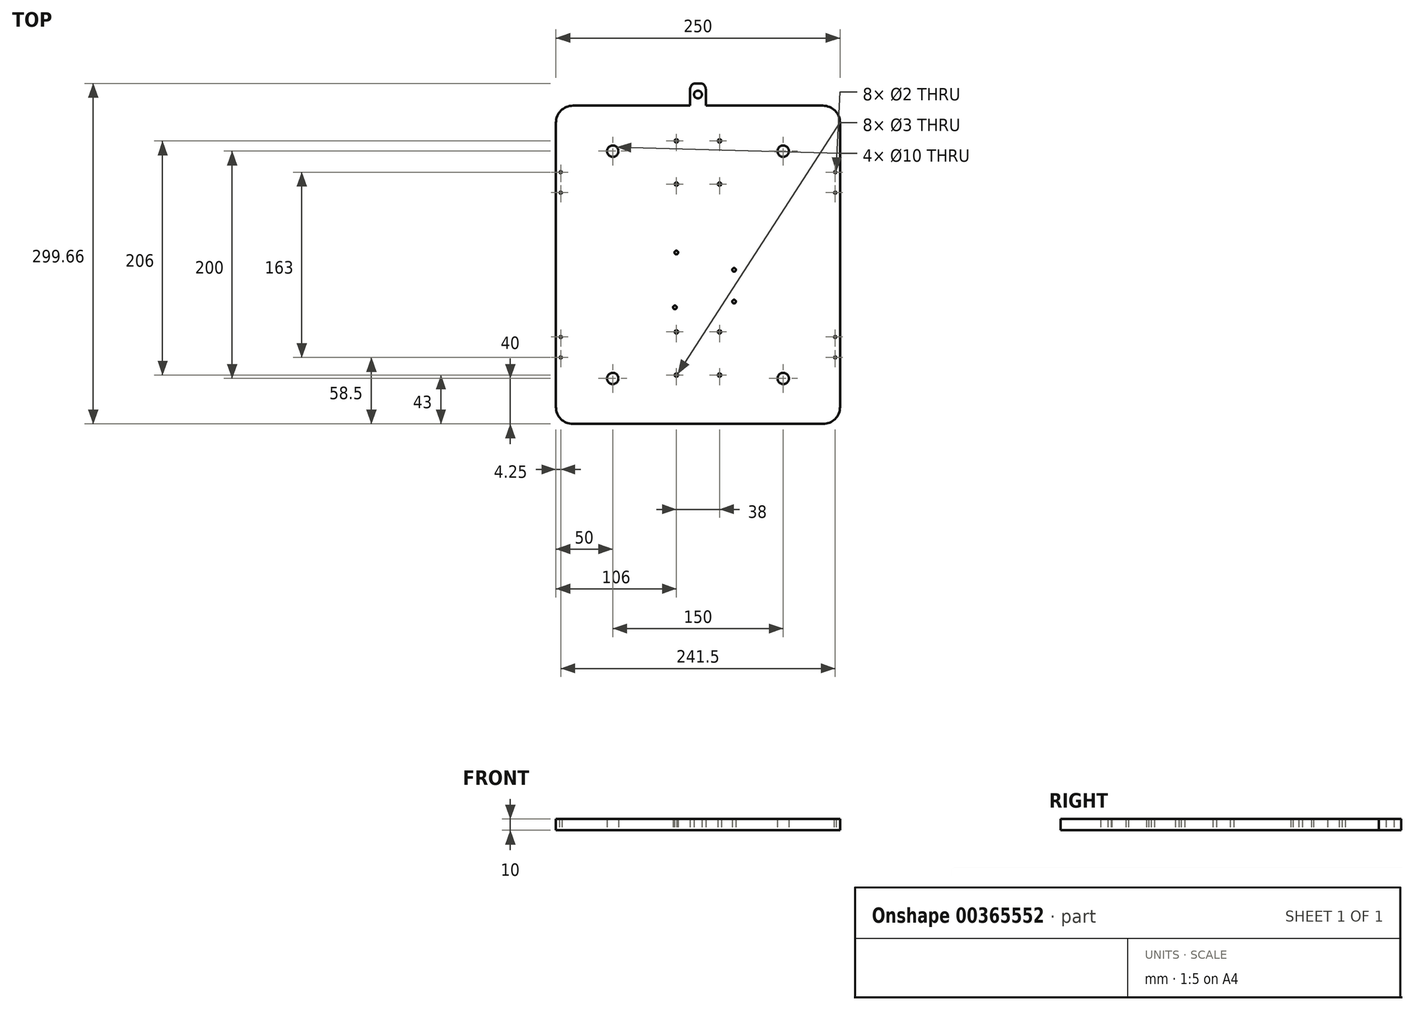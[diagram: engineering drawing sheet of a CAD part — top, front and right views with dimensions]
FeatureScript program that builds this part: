
annotation { "Feature Type Name" : "Feature", "Feature Type Description" : "" }
export const myFeature = defineFeature(function(context is Context, id is Id, definition is map)
    precondition{}
    {
        {
            var Q0;
            Q0=qCreatedBy(makeId("Top.planeOp"),FACE);
            var sketch = newSketch(context, id + "F0", { "sketchPlane" : qUnion([Q0])});
            skLineSegment(sketch, "E0.bottom", {"start": v(34.5, 17) * mm, "end": v(-34.5, 17) * mm});
            skLineSegment(sketch, "E0.top", {"start": v(34.5, -17) * mm, "end": v(-34.5, -17) * mm});
            skLineSegment(sketch, "E0.left", {"start": v(34.5, 17) * mm, "end": v(34.5, -17) * mm});
            skLineSegment(sketch, "E0.right", {"start": v(-34.5, 17) * mm, "end": v(-34.5, -17) * mm});
            skPoint(sketch, "E0.middle", {"position": v(0, 0) * mm});
            skSolve(sketch);
        }
        {
            var Q0;
            Q0=qCreatedBy(makeId("Top.planeOp"),FACE);
            var sketch = newSketch(context, id + "F1", { "sketchPlane" : qUnion([Q0])});
            skLineSegment(sketch, "E1.bottom", {"start": v(-110, 140) * mm, "end": v(-6.85, 140) * mm});
            skLineSegment(sketch, "E1.top", {"start": v(-110, -140) * mm, "end": v(110, -140) * mm});
            skLineSegment(sketch, "E1.left", {"start": v(-125, 125) * mm, "end": v(-125, -125) * mm});
            skLineSegment(sketch, "E1.right", {"start": v(125, 125) * mm, "end": v(125, -125) * mm});
            skPoint(sketch, "E1.middle", {"position": v(0, 0) * mm});
            skCircle(sketch, "E2", {"center": v(-120.75, 81.5) * mm, "radius": 1 * mm});
            skCircle(sketch, "E3", {"center": v(-120.75, 63.5) * mm, "radius": 1 * mm});
            skLineSegment(sketch, "E4", {"start": v(-120.75, 63.5) * mm, "end": v(-120.75, 81.5) * mm, "construction": true});
            skLineSegment(sketch, "E5.bottom", {"start": v(-107.7, 80) * mm, "end": v(-107.7, 65) * mm, "construction": true});
            skLineSegment(sketch, "E5.top", {"start": v(-125, 80) * mm, "end": v(-125, 65) * mm, "construction": true});
            skLineSegment(sketch, "E5.left", {"start": v(-107.7, 80) * mm, "end": v(-125, 80) * mm, "construction": true});
            skLineSegment(sketch, "E5.right", {"start": v(-107.7, 65) * mm, "end": v(-125, 65) * mm, "construction": true});
            skPoint(sketch, "E5.middle", {"position": v(-116.35, 72.5) * mm});
            skLineSegment(sketch, "E6", {"start": v(-125, 65) * mm, "end": v(-120.75, 65) * mm, "construction": true});
            skPoint(sketch, "E7", {"position": v(-120.75, 72.5) * mm});
            skPoint(sketch, "E8", {"position": v(-125, 72.5) * mm});
            skCircle(sketch, "E9.MirrorC", {"center": v(120.75, 81.5) * mm, "radius": 1 * mm});
            skCircle(sketch, "E10.MirrorC", {"center": v(120.75, 63.5) * mm, "radius": 1 * mm});
            skCircle(sketch, "E11.MirrorC", {"center": v(-120.75, -81.5) * mm, "radius": 1 * mm});
            skCircle(sketch, "E12.MirrorC", {"center": v(-120.75, -63.5) * mm, "radius": 1 * mm});
            skCircle(sketch, "E13.MirrorC", {"center": v(120.75, -81.5) * mm, "radius": 1 * mm});
            skCircle(sketch, "E14.MirrorC", {"center": v(120.75, -63.5) * mm, "radius": 1 * mm});
            skPoint(sketch, "E15", {"position": v(-107.7, 72.5) * mm});
            skCircle(sketch, "E16", {"center": v(-75, 100) * mm, "radius": 5 * mm});
            skCircle(sketch, "E17.MirrorC", {"center": v(75, 100) * mm, "radius": 5 * mm});
            skCircle(sketch, "E18", {"center": v(-75, -100) * mm, "radius": 5 * mm});
            skCircle(sketch, "E19.MirrorC", {"center": v(75, -100) * mm, "radius": 5 * mm});
            skPoint(sketch, "E20.visualSharp", {"position": v(-125, 140) * mm});
            skArc(sketch, "E20.filletArc", {"start": v(-110, 140) * mm, "mid": v(-120.6, 135.6) * mm, "end": v(-125, 125) * mm});
            skPoint(sketch, "E21.visualSharp", {"position": v(125, 140) * mm});
            skArc(sketch, "E21.filletArc", {"start": v(125, 125) * mm, "mid": v(120.6, 135.6) * mm, "end": v(110, 140) * mm});
            skPoint(sketch, "E22.visualSharp", {"position": v(-125, -140) * mm});
            skArc(sketch, "E22.filletArc", {"start": v(-125, -125) * mm, "mid": v(-120.6, -135.6) * mm, "end": v(-110, -140) * mm});
            skPoint(sketch, "E23.visualSharp", {"position": v(125, -140) * mm});
            skArc(sketch, "E23.filletArc", {"start": v(110, -140) * mm, "mid": v(120.6, -135.6) * mm, "end": v(125, -125) * mm});
            skLineSegment(sketch, "E24.bottom", {"start": v(34.3, 13.34) * mm, "end": v(-34.3, 13.34) * mm, "construction": true});
            skLineSegment(sketch, "E24.top", {"start": v(34.3, -40) * mm, "end": v(-34.29, -40) * mm, "construction": true});
            skLineSegment(sketch, "E24.left", {"start": v(34.29, 13.34) * mm, "end": v(34.29, -40) * mm, "construction": true});
            skLineSegment(sketch, "E24.right", {"start": v(-34.3, 13.34) * mm, "end": v(-34.3, -40) * mm, "construction": true});
            skCircle(sketch, "E25", {"center": v(-19.05, 10.8) * mm, "radius": 1.59 * mm});
            skLineSegment(sketch, "E26", {"start": v(-19.05, 10.8) * mm, "end": v(31.75, 10.8) * mm, "construction": true});
            skLineSegment(sketch, "E27", {"start": v(31.75, 10.8) * mm, "end": v(31.75, -4.44) * mm, "construction": true});
            skLineSegment(sketch, "E28", {"start": v(31.75, -4.44) * mm, "end": v(31.75, -32.38) * mm, "construction": true});
            skCircle(sketch, "E29", {"center": v(31.75, -4.44) * mm, "radius": 1.59 * mm});
            skCircle(sketch, "E30", {"center": v(31.75, -32.38) * mm, "radius": 1.59 * mm});
            skLineSegment(sketch, "E31", {"start": v(-19.05, 10.8) * mm, "end": v(-20.32, 10.8) * mm, "construction": true});
            skLineSegment(sketch, "E32", {"start": v(-20.32, 10.8) * mm, "end": v(-20.32, -37.46) * mm, "construction": true});
            skCircle(sketch, "E33", {"center": v(-20.32, -37.46) * mm, "radius": 1.59 * mm});
            skLineSegment(sketch, "E34", {"start": v(-20.32, -37.46) * mm, "end": v(-20.32, -40) * mm, "construction": true});
            skLineSegment(sketch, "E35", {"start": v(-20.32, -40) * mm, "end": v(-34.29, -40) * mm, "construction": true});
            skPoint(sketch, "E36", {"position": v(-34.3, -13.33) * mm});
            skPoint(sketch, "E37", {"position": v(0, 13.34) * mm});
            skLineSegment(sketch, "E38", {"start": v(0, 13.34) * mm, "end": v(0, -13.33) * mm, "construction": true});
            skLineSegment(sketch, "E39", {"start": v(0, -13.33) * mm, "end": v(-34.3, -13.33) * mm, "construction": true});
            skLineSegment(sketch, "E40.bottom", {"start": v(22, 112) * mm, "end": v(-22, 112) * mm, "construction": true});
            skLineSegment(sketch, "E40.top", {"start": v(22, 68) * mm, "end": v(-22, 68) * mm, "construction": true});
            skLineSegment(sketch, "E40.left", {"start": v(22, 112) * mm, "end": v(22, 68) * mm, "construction": true});
            skLineSegment(sketch, "E40.right", {"start": v(-22, 112) * mm, "end": v(-22, 68) * mm, "construction": true});
            skPoint(sketch, "E40.middle", {"position": v(0, 90) * mm});
            skLineSegment(sketch, "E41", {"start": v(-22, 71) * mm, "end": v(-19, 71) * mm, "construction": true});
            skLineSegment(sketch, "E42", {"start": v(-19, 71) * mm, "end": v(-19, 68) * mm, "construction": true});
            skCircle(sketch, "E43", {"center": v(-19, 71) * mm, "radius": 1.5 * mm});
            skCircle(sketch, "E44.MirrorC", {"center": v(19, 71) * mm, "radius": 1.5 * mm});
            skCircle(sketch, "E45.MirrorC", {"center": v(-19, 109) * mm, "radius": 1.5 * mm});
            skCircle(sketch, "E46.MirrorC", {"center": v(19, 109) * mm, "radius": 1.5 * mm});
            skLineSegment(sketch, "E47.bottom", {"start": v(22, -56) * mm, "end": v(-22, -56) * mm, "construction": true});
            skLineSegment(sketch, "E47.top", {"start": v(22, -100) * mm, "end": v(-22, -100) * mm, "construction": true});
            skLineSegment(sketch, "E47.left", {"start": v(22, -56) * mm, "end": v(22, -100) * mm, "construction": true});
            skLineSegment(sketch, "E47.right", {"start": v(-22, -56) * mm, "end": v(-22, -100) * mm, "construction": true});
            skPoint(sketch, "E47.middle", {"position": v(0, -78) * mm});
            skLineSegment(sketch, "E48", {"start": v(-22, -97) * mm, "end": v(-19, -97) * mm, "construction": true});
            skLineSegment(sketch, "E49", {"start": v(-19, -97) * mm, "end": v(-19, -100) * mm, "construction": true});
            skCircle(sketch, "E50", {"center": v(-19, -97) * mm, "radius": 1.5 * mm});
            skCircle(sketch, "E51.MirrorC", {"center": v(19, -97) * mm, "radius": 1.5 * mm});
            skCircle(sketch, "E52.MirrorC", {"center": v(-19, -59) * mm, "radius": 1.5 * mm});
            skCircle(sketch, "E53.MirrorC", {"center": v(19, -59) * mm, "radius": 1.5 * mm});
            skLineSegment(sketch, "E54.bottom", {"start": v(-209.95, 111.77) * mm, "end": v(-204.95, 111.77) * mm});
            skLineSegment(sketch, "E54.top", {"start": v(-209.95, 43.77) * mm, "end": v(-204.95, 43.77) * mm});
            skLineSegment(sketch, "E54.left", {"start": v(-209.95, 111.77) * mm, "end": v(-209.95, 43.77) * mm});
            skLineSegment(sketch, "E54.right", {"start": v(-204.95, 111.77) * mm, "end": v(-204.95, 43.77) * mm});
            skLineSegment(sketch, "E55.bottom", {"start": v(-196.24, 112) * mm, "end": v(-191.24, 112) * mm});
            skLineSegment(sketch, "E55.top", {"start": v(-196.24, 44) * mm, "end": v(-191.24, 44) * mm});
            skLineSegment(sketch, "E55.left", {"start": v(-196.24, 112) * mm, "end": v(-196.24, 44) * mm});
            skLineSegment(sketch, "E55.right", {"start": v(-191.24, 112) * mm, "end": v(-191.24, 44) * mm});
            skLineSegment(sketch, "E56.bottom", {"start": v(-227.86, 102.42) * mm, "end": v(-222.86, 102.42) * mm});
            skLineSegment(sketch, "E56.top", {"start": v(-227.86, 54.92) * mm, "end": v(-222.86, 54.92) * mm});
            skLineSegment(sketch, "E56.left", {"start": v(-227.86, 102.42) * mm, "end": v(-227.86, 54.92) * mm});
            skLineSegment(sketch, "E56.right", {"start": v(-222.86, 102.42) * mm, "end": v(-222.86, 54.92) * mm});
            skLineSegment(sketch, "E57.bottom", {"start": v(-219.6, 102.78) * mm, "end": v(-214.6, 102.78) * mm});
            skLineSegment(sketch, "E57.top", {"start": v(-219.6, 55.28) * mm, "end": v(-214.6, 55.28) * mm});
            skLineSegment(sketch, "E57.left", {"start": v(-219.6, 102.78) * mm, "end": v(-219.6, 55.28) * mm});
            skLineSegment(sketch, "E57.right", {"start": v(-214.6, 102.78) * mm, "end": v(-214.6, 55.28) * mm});
            skLineSegment(sketch, "E58.bottom", {"start": v(-170.22, 112.13) * mm, "end": v(-165.22, 112.13) * mm});
            skLineSegment(sketch, "E58.top", {"start": v(-170.22, 44.13) * mm, "end": v(-165.22, 44.13) * mm});
            skLineSegment(sketch, "E58.left", {"start": v(-170.22, 112.13) * mm, "end": v(-170.22, 44.13) * mm});
            skLineSegment(sketch, "E58.right", {"start": v(-165.22, 112.13) * mm, "end": v(-165.22, 44.13) * mm});
            skLineSegment(sketch, "E59.bottom", {"start": v(-156.51, 112.37) * mm, "end": v(-151.51, 112.37) * mm});
            skLineSegment(sketch, "E59.top", {"start": v(-156.51, 44.37) * mm, "end": v(-151.51, 44.37) * mm});
            skLineSegment(sketch, "E59.left", {"start": v(-156.51, 112.37) * mm, "end": v(-156.51, 44.37) * mm});
            skLineSegment(sketch, "E59.right", {"start": v(-151.51, 112.37) * mm, "end": v(-151.51, 44.37) * mm});
            skLineSegment(sketch, "E60.bottom", {"start": v(-188.14, 102.78) * mm, "end": v(-183.14, 102.78) * mm});
            skLineSegment(sketch, "E60.top", {"start": v(-188.14, 55.28) * mm, "end": v(-183.14, 55.28) * mm});
            skLineSegment(sketch, "E60.left", {"start": v(-188.14, 102.78) * mm, "end": v(-188.14, 55.28) * mm});
            skLineSegment(sketch, "E60.right", {"start": v(-183.14, 102.78) * mm, "end": v(-183.14, 55.28) * mm});
            skLineSegment(sketch, "E61.bottom", {"start": v(-179.87, 103.15) * mm, "end": v(-174.87, 103.15) * mm});
            skLineSegment(sketch, "E61.top", {"start": v(-179.87, 55.65) * mm, "end": v(-174.87, 55.65) * mm});
            skLineSegment(sketch, "E61.left", {"start": v(-179.87, 103.15) * mm, "end": v(-179.87, 55.65) * mm});
            skLineSegment(sketch, "E61.right", {"start": v(-174.87, 103.15) * mm, "end": v(-174.87, 55.65) * mm});
            skLineSegment(sketch, "E62.bottom", {"start": v(-170.25, 38.66) * mm, "end": v(-165.25, 38.66) * mm});
            skLineSegment(sketch, "E62.top", {"start": v(-170.25, -29.34) * mm, "end": v(-165.25, -29.34) * mm});
            skLineSegment(sketch, "E62.left", {"start": v(-170.25, 38.66) * mm, "end": v(-170.25, -29.34) * mm});
            skLineSegment(sketch, "E62.right", {"start": v(-165.25, 38.66) * mm, "end": v(-165.25, -29.34) * mm});
            skLineSegment(sketch, "E63.bottom", {"start": v(-156.54, 38.9) * mm, "end": v(-151.54, 38.9) * mm});
            skLineSegment(sketch, "E63.top", {"start": v(-156.54, -29.1) * mm, "end": v(-151.54, -29.1) * mm});
            skLineSegment(sketch, "E63.left", {"start": v(-156.54, 38.9) * mm, "end": v(-156.54, -29.1) * mm});
            skLineSegment(sketch, "E63.right", {"start": v(-151.54, 38.9) * mm, "end": v(-151.54, -29.1) * mm});
            skLineSegment(sketch, "E64.bottom", {"start": v(-188.16, 29.31) * mm, "end": v(-183.16, 29.31) * mm});
            skLineSegment(sketch, "E64.top", {"start": v(-188.16, -18.19) * mm, "end": v(-183.16, -18.19) * mm});
            skLineSegment(sketch, "E64.left", {"start": v(-188.16, 29.31) * mm, "end": v(-188.16, -18.19) * mm});
            skLineSegment(sketch, "E64.right", {"start": v(-183.16, 29.31) * mm, "end": v(-183.16, -18.19) * mm});
            skLineSegment(sketch, "E65.bottom", {"start": v(-179.9, 29.68) * mm, "end": v(-174.9, 29.68) * mm});
            skLineSegment(sketch, "E65.top", {"start": v(-179.9, -17.82) * mm, "end": v(-174.9, -17.82) * mm});
            skLineSegment(sketch, "E65.left", {"start": v(-179.9, 29.68) * mm, "end": v(-179.9, -17.82) * mm});
            skLineSegment(sketch, "E65.right", {"start": v(-174.9, 29.68) * mm, "end": v(-174.9, -17.82) * mm});
            skLineSegment(sketch, "E66.bottom", {"start": v(-147.22, -11.4) * mm, "end": v(-142.22, -11.4) * mm});
            skLineSegment(sketch, "E66.top", {"start": v(-147.22, -90.4) * mm, "end": v(-142.22, -90.4) * mm});
            skLineSegment(sketch, "E66.left", {"start": v(-147.22, -11.4) * mm, "end": v(-147.22, -90.4) * mm});
            skLineSegment(sketch, "E66.right", {"start": v(-142.22, -11.4) * mm, "end": v(-142.22, -90.4) * mm});
            skLineSegment(sketch, "E67.bottom", {"start": v(-137.22, -10.94) * mm, "end": v(-132.22, -10.94) * mm});
            skLineSegment(sketch, "E67.top", {"start": v(-137.22, -89.94) * mm, "end": v(-132.22, -89.94) * mm});
            skLineSegment(sketch, "E67.left", {"start": v(-137.22, -10.94) * mm, "end": v(-137.22, -89.94) * mm});
            skLineSegment(sketch, "E67.right", {"start": v(-132.22, -10.94) * mm, "end": v(-132.22, -89.94) * mm});
            skLineSegment(sketch, "E68.bottom", {"start": v(-165.26, -36.1) * mm, "end": v(-160.26, -36.1) * mm});
            skLineSegment(sketch, "E68.top", {"start": v(-165.26, -70.1) * mm, "end": v(-160.26, -70.1) * mm});
            skLineSegment(sketch, "E68.left", {"start": v(-165.26, -36.1) * mm, "end": v(-165.26, -70.1) * mm});
            skLineSegment(sketch, "E68.right", {"start": v(-160.26, -36.1) * mm, "end": v(-160.26, -70.1) * mm});
            skLineSegment(sketch, "E69.bottom", {"start": v(-156.3, -36.38) * mm, "end": v(-151.3, -36.38) * mm});
            skLineSegment(sketch, "E69.top", {"start": v(-156.3, -70.38) * mm, "end": v(-151.3, -70.38) * mm});
            skLineSegment(sketch, "E69.left", {"start": v(-156.3, -36.38) * mm, "end": v(-156.3, -70.38) * mm});
            skLineSegment(sketch, "E69.right", {"start": v(-151.3, -36.38) * mm, "end": v(-151.3, -70.38) * mm});
            skLineSegment(sketch, "E70.bottom", {"start": v(-152.22, -153.4) * mm, "end": v(-157.22, -153.4) * mm});
            skLineSegment(sketch, "E70.top", {"start": v(-152.22, -74.4) * mm, "end": v(-157.22, -74.4) * mm});
            skLineSegment(sketch, "E70.left", {"start": v(-152.22, -153.4) * mm, "end": v(-152.22, -74.4) * mm});
            skLineSegment(sketch, "E70.right", {"start": v(-157.22, -153.4) * mm, "end": v(-157.22, -74.4) * mm});
            skLineSegment(sketch, "E71.bottom", {"start": v(-162.22, -153.86) * mm, "end": v(-167.22, -153.86) * mm});
            skLineSegment(sketch, "E71.top", {"start": v(-162.22, -74.86) * mm, "end": v(-167.22, -74.86) * mm});
            skLineSegment(sketch, "E71.left", {"start": v(-162.22, -153.86) * mm, "end": v(-162.22, -74.86) * mm});
            skLineSegment(sketch, "E71.right", {"start": v(-167.22, -153.86) * mm, "end": v(-167.22, -74.86) * mm});
            skLineSegment(sketch, "E72.bottom", {"start": v(-134.19, -128.69) * mm, "end": v(-139.19, -128.69) * mm});
            skLineSegment(sketch, "E72.top", {"start": v(-134.19, -94.69) * mm, "end": v(-139.19, -94.69) * mm});
            skLineSegment(sketch, "E72.left", {"start": v(-134.19, -128.69) * mm, "end": v(-134.19, -94.69) * mm});
            skLineSegment(sketch, "E72.right", {"start": v(-139.19, -128.69) * mm, "end": v(-139.19, -94.69) * mm});
            skLineSegment(sketch, "E73.bottom", {"start": v(-143.15, -128.41) * mm, "end": v(-148.15, -128.41) * mm});
            skLineSegment(sketch, "E73.top", {"start": v(-143.15, -94.41) * mm, "end": v(-148.15, -94.41) * mm});
            skLineSegment(sketch, "E73.left", {"start": v(-143.15, -128.41) * mm, "end": v(-143.15, -94.41) * mm});
            skLineSegment(sketch, "E73.right", {"start": v(-148.15, -128.41) * mm, "end": v(-148.15, -94.41) * mm});
            skPoint(sketch, "E74", {"position": v(0, 140) * mm});
            skLineSegment(sketch, "E75.top", {"start": v(1.85, 159.66) * mm, "end": v(-1.85, 159.66) * mm});
            skLineSegment(sketch, "E75.left", {"start": v(6.85, 140) * mm, "end": v(6.85, 154.66) * mm});
            skLineSegment(sketch, "E75.right", {"start": v(-6.85, 140) * mm, "end": v(-6.85, 154.66) * mm});
            skPoint(sketch, "E75.middle", {"position": v(0, 149.83) * mm});
            skCircle(sketch, "E76", {"center": v(0, 149.83) * mm, "radius": 3.43 * mm});
            skPoint(sketch, "E77.visualSharp", {"position": v(-6.85, 159.66) * mm});
            skArc(sketch, "E77.filletArc", {"start": v(-1.85, 159.66) * mm, "mid": v(-5.39, 158.2) * mm, "end": v(-6.85, 154.66) * mm});
            skPoint(sketch, "E78.visualSharp", {"position": v(6.85, 159.66) * mm});
            skArc(sketch, "E78.filletArc", {"start": v(6.85, 154.66) * mm, "mid": v(5.39, 158.2) * mm, "end": v(1.85, 159.66) * mm});
            skLineSegment(sketch, "E79.trimOffspring", {"start": v(6.85, 140) * mm, "end": v(110, 140) * mm});
            skLineSegment(sketch, "E80.bottom", {"start": v(-210.3, 39.28) * mm, "end": v(-205.3, 39.28) * mm});
            skLineSegment(sketch, "E80.top", {"start": v(-210.3, -28.72) * mm, "end": v(-205.3, -28.72) * mm});
            skLineSegment(sketch, "E80.left", {"start": v(-210.3, 39.28) * mm, "end": v(-210.3, -28.72) * mm});
            skLineSegment(sketch, "E80.right", {"start": v(-205.3, 39.28) * mm, "end": v(-205.3, -28.72) * mm});
            skLineSegment(sketch, "E81.bottom", {"start": v(-196.6, 39.52) * mm, "end": v(-191.6, 39.52) * mm});
            skLineSegment(sketch, "E81.top", {"start": v(-196.6, -28.48) * mm, "end": v(-191.6, -28.48) * mm});
            skLineSegment(sketch, "E81.left", {"start": v(-196.6, 39.52) * mm, "end": v(-196.6, -28.48) * mm});
            skLineSegment(sketch, "E81.right", {"start": v(-191.6, 39.52) * mm, "end": v(-191.6, -28.48) * mm});
            skLineSegment(sketch, "E82.bottom", {"start": v(-228.22, 29.93) * mm, "end": v(-223.22, 29.93) * mm});
            skLineSegment(sketch, "E82.top", {"start": v(-228.22, -17.57) * mm, "end": v(-223.22, -17.57) * mm});
            skLineSegment(sketch, "E82.left", {"start": v(-228.22, 29.93) * mm, "end": v(-228.22, -17.57) * mm});
            skLineSegment(sketch, "E82.right", {"start": v(-223.22, 29.93) * mm, "end": v(-223.22, -17.57) * mm});
            skLineSegment(sketch, "E83.bottom", {"start": v(-219.96, 30.3) * mm, "end": v(-214.96, 30.3) * mm});
            skLineSegment(sketch, "E83.top", {"start": v(-219.96, -17.2) * mm, "end": v(-214.96, -17.2) * mm});
            skLineSegment(sketch, "E83.left", {"start": v(-219.96, 30.3) * mm, "end": v(-219.96, -17.2) * mm});
            skLineSegment(sketch, "E83.right", {"start": v(-214.96, 30.3) * mm, "end": v(-214.96, -17.2) * mm});
            skSolve(sketch);
        }
        {
            var Q0;
            Q0=makeQuery(id+"F1.imprint","IMPRINT",FACE,{"disambiguationData":[TD([[makeQuery(id+"F1.imprint","IMPRINT",EDGE,{"derivedFrom":sQuery(id+"F1.wireOp",EDGE,"E1.bottom")}),-1.0]])]});
            extrude(context, id + "F2", {"entities" : qUnion([Q0]), "depth" : 10 * mm, "offsetDistance" : 25 * mm});
        }
    });
